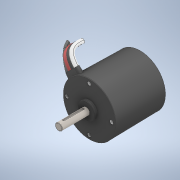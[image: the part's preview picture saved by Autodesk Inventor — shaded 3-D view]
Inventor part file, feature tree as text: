
AUTODESK INVENTOR PART (.ipt)
format: ipt  version: 2020 (Build 240168000, 168)  size: 463,360 bytes
history: native  units: in
note: dims shown in document units (in); Inventor stores cm internally (conversion verified against a paired STEP export)
features: boolean_combine x1, revolve x1, sketch x1
ambient origin geometry x8: Origin, YZ Plane, XZ Plane, XY Plane, X Axis, Y Axis, Z Axis, Center Point
bodies: Solid1 (feature_tree)
feature tree (3):
  boolean_combine  "Combine1"
  revolve  "Revolution1"  [1 undecoded]
  sketch  "Sketch2"  dims[d0=90.0deg]
note: 1 required parameter value undecoded (feature->parameter linkage not recoverable at this tier; creation-order binding heuristic only, values carry confidence <= 0.55)
